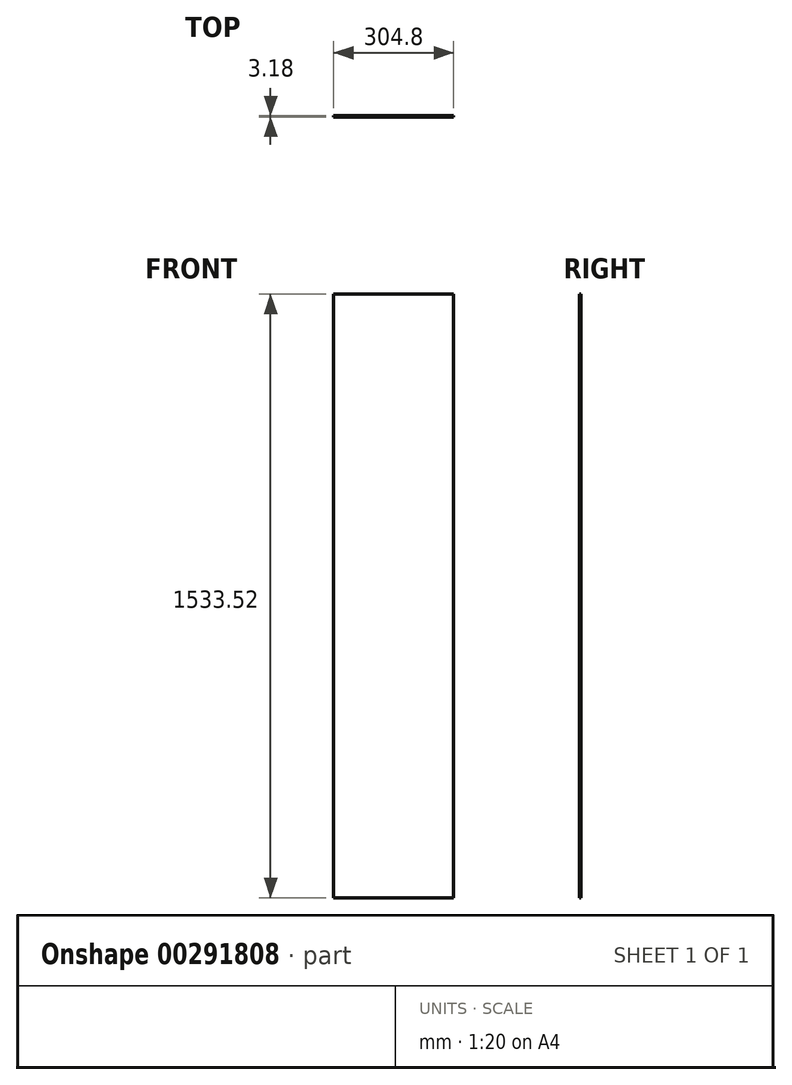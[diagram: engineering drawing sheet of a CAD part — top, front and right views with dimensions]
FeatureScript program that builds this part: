
annotation { "Feature Type Name" : "Feature", "Feature Type Description" : "" }
export const myFeature = defineFeature(function(context is Context, id is Id, definition is map)
    precondition{}
    {
        {
            var Q0;
            Q0=qCreatedBy(makeId("Front.planeOp"),FACE);
            var sketch = newSketch(context, id + "F0", { "sketchPlane" : qUnion([Q0])});
            skLineSegment(sketch, "E0.bottom", {"start": v(152.4, 766.76) * mm, "end": v(-152.4, 766.76) * mm});
            skLineSegment(sketch, "E0.top", {"start": v(152.4, -766.76) * mm, "end": v(-152.4, -766.76) * mm});
            skLineSegment(sketch, "E0.left", {"start": v(152.4, 766.76) * mm, "end": v(152.4, -766.76) * mm});
            skLineSegment(sketch, "E0.right", {"start": v(-152.4, 766.76) * mm, "end": v(-152.4, -766.76) * mm});
            skPoint(sketch, "E0.middle", {"position": v(0, 0) * mm});
            skSolve(sketch);
        }
        {
            var Q0;
            Q0 = qSketchRegion(id + "F0", true);
            extrude(context, id + "F1", {"entities" : qUnion([Q0]), "endBound" : BoundingType.SYMMETRIC, "depth" : 3.17 * mm});
        }
    });
